# Revit family: Drain_Slotted_Zurn-Z888-4
name_source: partatom
category: Plumbing Fixtures
units: mm (PartAtom-declared; Revit-internal decimal feet)

## family parameters
Always vertical = Yes
Cut with Voids When Loaded = No
Maintain Annotation Orientation = No
OmniClass Number = 23.70.50.21.24
OmniClass Title = Waste Water Drains
Part Type = Normal
Room Calculation Point = No
Round Connector Dimension = Use Radius
Shared = No
Work Plane-Based = No

## types (3) — shared parameters
Assembly Code = D2030300
CW Connection = No
Default Elevation = 20 "
Description = SLOTTED DRAINAGE SYSTEM FOR 4 [102] PIPE OR EQUIVALENT
HW Connection = No
Manufacturer = Zurn Water, LLC
Manufacurer Brand = Zurn
Model = Z888-4
Modified Date = 03/06/2026
Product Documentation Link = https://files.zurn.com
Product Page URL = https://www.zurn.com
Product data url = https://www.bimobject.com
URL = www.zurn.com
Vent Connection = No
WFU = 1
Waste Connection = Yes
zero-valued in all types: CWFU, HWFU

## per-type parameters (varying)
| type | Main Material | Nominal Diameter | Pipe Size 'A' (Inner Diameter) | Pipe Size 'A' (Inner Radius) | Pipe Size 'A' (Nominal Radius) | Pipe Size 'A' (Outer Diameter) | Pipe Size 'A' (Outer Radius) |
| Z888-4 with 4 Inch No-Hub End Outlet | Polymer - Zurn - HDPE - Black | 4 " | 4.028 " | 2.014 " | 2 " | 4.5 " | 2.25 " |
| Z888-4 with 3 Inch No-Hub End Outlet | Polymer - Zurn - HDPE - Black | 3 " | 3.068 " | 1.534 " | 1.5 " | 3.5 " | 1.75 " |
| Z888-4 with 2 Inch No-Hub End Outlet | Polymer - Zurn - LDPE - Black | 2 " | 2.067 " | 1.034 " | 1 " | 2.375 " | 1.188 " |

## geometry (parser evidence)
native form markers: Sweep x2
no freeform markers — native parametric forms only
